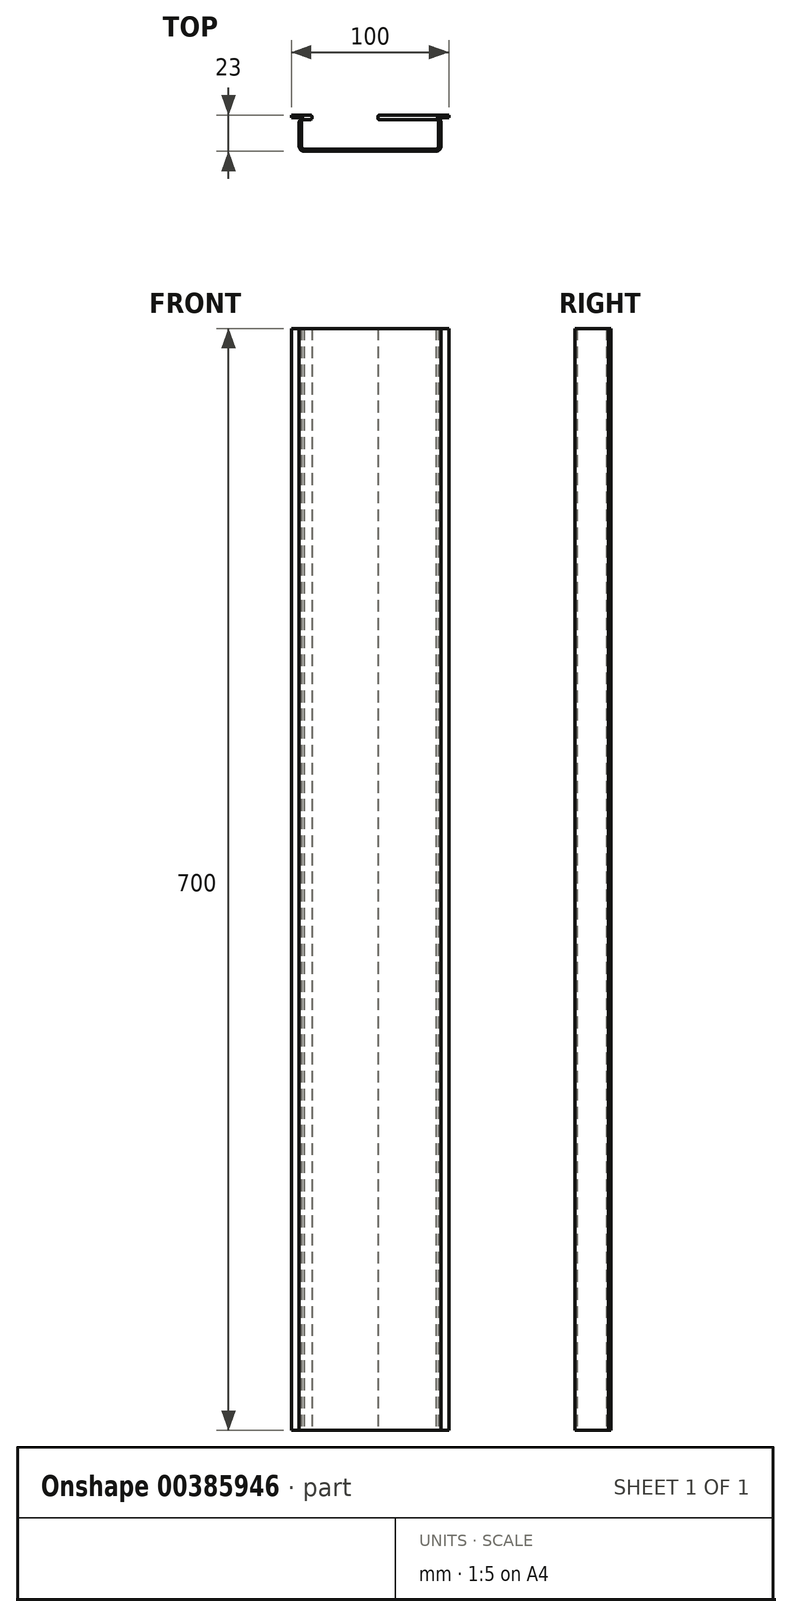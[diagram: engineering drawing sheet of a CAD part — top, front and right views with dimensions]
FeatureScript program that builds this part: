
annotation { "Feature Type Name" : "Feature", "Feature Type Description" : "" }
export const myFeature = defineFeature(function(context is Context, id is Id, definition is map)
    precondition{}
    {
        {
            var Q0;
            Q0=qCreatedBy(makeId("Top.planeOp"),FACE);
            var sketch = newSketch(context, id + "F0", { "sketchPlane" : qUnion([Q0])});
            skLineSegment(sketch, "E0", {"start": v(3, 0) * mm, "end": v(87, 0) * mm});
            skLineSegment(sketch, "E1", {"start": v(90, 3) * mm, "end": v(90, 18.5) * mm});
            skLineSegment(sketch, "E2", {"start": v(0, 3) * mm, "end": v(0, 18.5) * mm});
            skLineSegment(sketch, "E3.0", {"start": v(1.5, 3) * mm, "end": v(1.5, 18.5) * mm});
            skLineSegment(sketch, "E3.1", {"start": v(3, 1.5) * mm, "end": v(87, 1.5) * mm});
            skLineSegment(sketch, "E3.2", {"start": v(88.5, 3) * mm, "end": v(88.5, 18.5) * mm});
            skLineSegment(sketch, "E4", {"start": v(1.5, 21.5) * mm, "end": v(0, 21.5) * mm});
            skLineSegment(sketch, "E5", {"start": v(90, 21.5) * mm, "end": v(88.5, 21.5) * mm});
            skLineSegment(sketch, "E6.bottom", {"start": v(50, 21.5) * mm, "end": v(95, 21.5) * mm});
            skLineSegment(sketch, "E6.top", {"start": v(50, 23) * mm, "end": v(95, 23) * mm});
            skLineSegment(sketch, "E6.left", {"start": v(50, 20) * mm, "end": v(50, 21.5) * mm});
            skLineSegment(sketch, "E6.right", {"start": v(95, 21.5) * mm, "end": v(95, 21.5) * mm});
            skPoint(sketch, "E7.visualSharp", {"position": v(95, 23) * mm});
            skPoint(sketch, "E8.visualSharp", {"position": v(50, 23) * mm});
            skLineSegment(sketch, "E9.bottom", {"start": v(8, 21.5) * mm, "end": v(-5, 21.5) * mm});
            skLineSegment(sketch, "E9.top", {"start": v(8, 23) * mm, "end": v(-5, 23) * mm});
            skLineSegment(sketch, "E9.left", {"start": v(8, 20) * mm, "end": v(8, 21.5) * mm});
            skLineSegment(sketch, "E9.right", {"start": v(-5, 21.5) * mm, "end": v(-5, 21.5) * mm});
            skPoint(sketch, "E10.visualSharp", {"position": v(-5, 23) * mm});
            skPoint(sketch, "E11.visualSharp", {"position": v(8, 23) * mm});
            skLineSegment(sketch, "E12", {"start": v(-5, 21.5) * mm, "end": v(-5, 23) * mm});
            skLineSegment(sketch, "E13", {"start": v(8, 21.5) * mm, "end": v(8, 23) * mm});
            skLineSegment(sketch, "E14", {"start": v(50, 23) * mm, "end": v(50, 21.5) * mm});
            skLineSegment(sketch, "E15", {"start": v(95, 23) * mm, "end": v(95, 21.5) * mm});
            skLineSegment(sketch, "E16", {"start": v(3, 21.5) * mm, "end": v(8, 21.5) * mm});
            skLineSegment(sketch, "E17.0", {"start": v(3, 20) * mm, "end": v(8, 20) * mm});
            skLineSegment(sketch, "E18", {"start": v(87, 21.5) * mm, "end": v(50, 21.5) * mm});
            skLineSegment(sketch, "E19", {"start": v(50, 21.5) * mm, "end": v(50, 20) * mm});
            skLineSegment(sketch, "E20", {"start": v(50, 20) * mm, "end": v(87, 20) * mm});
            skPoint(sketch, "E21.visualSharp", {"position": v(1.5, 1.5) * mm});
            skArc(sketch, "E21.filletArc", {"start": v(1.5, 3) * mm, "mid": v(1.94, 1.94) * mm, "end": v(3, 1.5) * mm});
            skPoint(sketch, "E22.visualSharp", {"position": v(88.5, 1.5) * mm});
            skArc(sketch, "E22.filletArc", {"start": v(87, 1.5) * mm, "mid": v(88.06, 1.94) * mm, "end": v(88.5, 3) * mm});
            skPoint(sketch, "E23.visualSharp", {"position": v(90, 0) * mm});
            skArc(sketch, "E23.filletArc", {"start": v(87, 0) * mm, "mid": v(89.12, 0.88) * mm, "end": v(90, 3) * mm});
            skPoint(sketch, "E24.visualSharp", {"position": v(0, 0) * mm});
            skArc(sketch, "E24.filletArc", {"start": v(0, 3) * mm, "mid": v(0.88, 0.88) * mm, "end": v(3, 0) * mm});
            skPoint(sketch, "E25.visualSharp", {"position": v(1.5, 20) * mm});
            skArc(sketch, "E25.filletArc", {"start": v(3, 20) * mm, "mid": v(1.94, 19.56) * mm, "end": v(1.5, 18.5) * mm});
            skPoint(sketch, "E26.visualSharp", {"position": v(0, 21.5) * mm});
            skArc(sketch, "E26.filletArc", {"start": v(3, 21.5) * mm, "mid": v(0.88, 20.62) * mm, "end": v(0, 18.5) * mm});
            skPoint(sketch, "E27.visualSharp", {"position": v(88.5, 20) * mm});
            skArc(sketch, "E27.filletArc", {"start": v(88.5, 18.5) * mm, "mid": v(88.06, 19.56) * mm, "end": v(87, 20) * mm});
            skPoint(sketch, "E28.visualSharp", {"position": v(90, 21.5) * mm});
            skArc(sketch, "E28.filletArc", {"start": v(90, 18.5) * mm, "mid": v(89.12, 20.62) * mm, "end": v(87, 21.5) * mm});
            skSolve(sketch);
        }
        {
            var Q0;
            Q0 = qSketchRegion(id + "F0", true);
            extrude(context, id + "F1", {"entities" : qUnion([Q0]), "endBound" : BoundingType.SYMMETRIC, "depth" : 700 * mm});
        }
        {
            var Q0;
            Q0=makeQuery(id+"F1.opExtrude","SWEPT_EDGE",EDGE,{"disambiguationData":[OSD([sQuery(id+"F0.wireOp",EDGE,"E6.top"),sQuery(id+"F0.wireOp",EDGE,"E14")])]});
            var Q1;
            Q1=makeQuery(id+"F1.opExtrude","SWEPT_EDGE",EDGE,{"disambiguationData":[OSD([sQuery(id+"F0.wireOp",EDGE,"E19"),sQuery(id+"F0.wireOp",EDGE,"E20")])]});
            var Q2;
            Q2=makeQuery(id+"F1.opExtrude","SWEPT_EDGE",EDGE,{"disambiguationData":[OSD([sQuery(id+"F0.wireOp",EDGE,"E9.top"),sQuery(id+"F0.wireOp",EDGE,"E13")])]});
            var Q3;
            Q3=makeQuery(id+"F1.opExtrude","SWEPT_EDGE",EDGE,{"disambiguationData":[OSD([sQuery(id+"F0.wireOp",EDGE,"E17.0"),sQuery(id+"F0.wireOp",EDGE,"E9.left")])]});
            fillet(context, id + "F2", {"entities" : qUnion([Q0, Q1, Q2, Q3]), "radius" : 1 * mm, "tangentPropagation" : true, "allowEdgeOverflow" : false});
        }
    });
